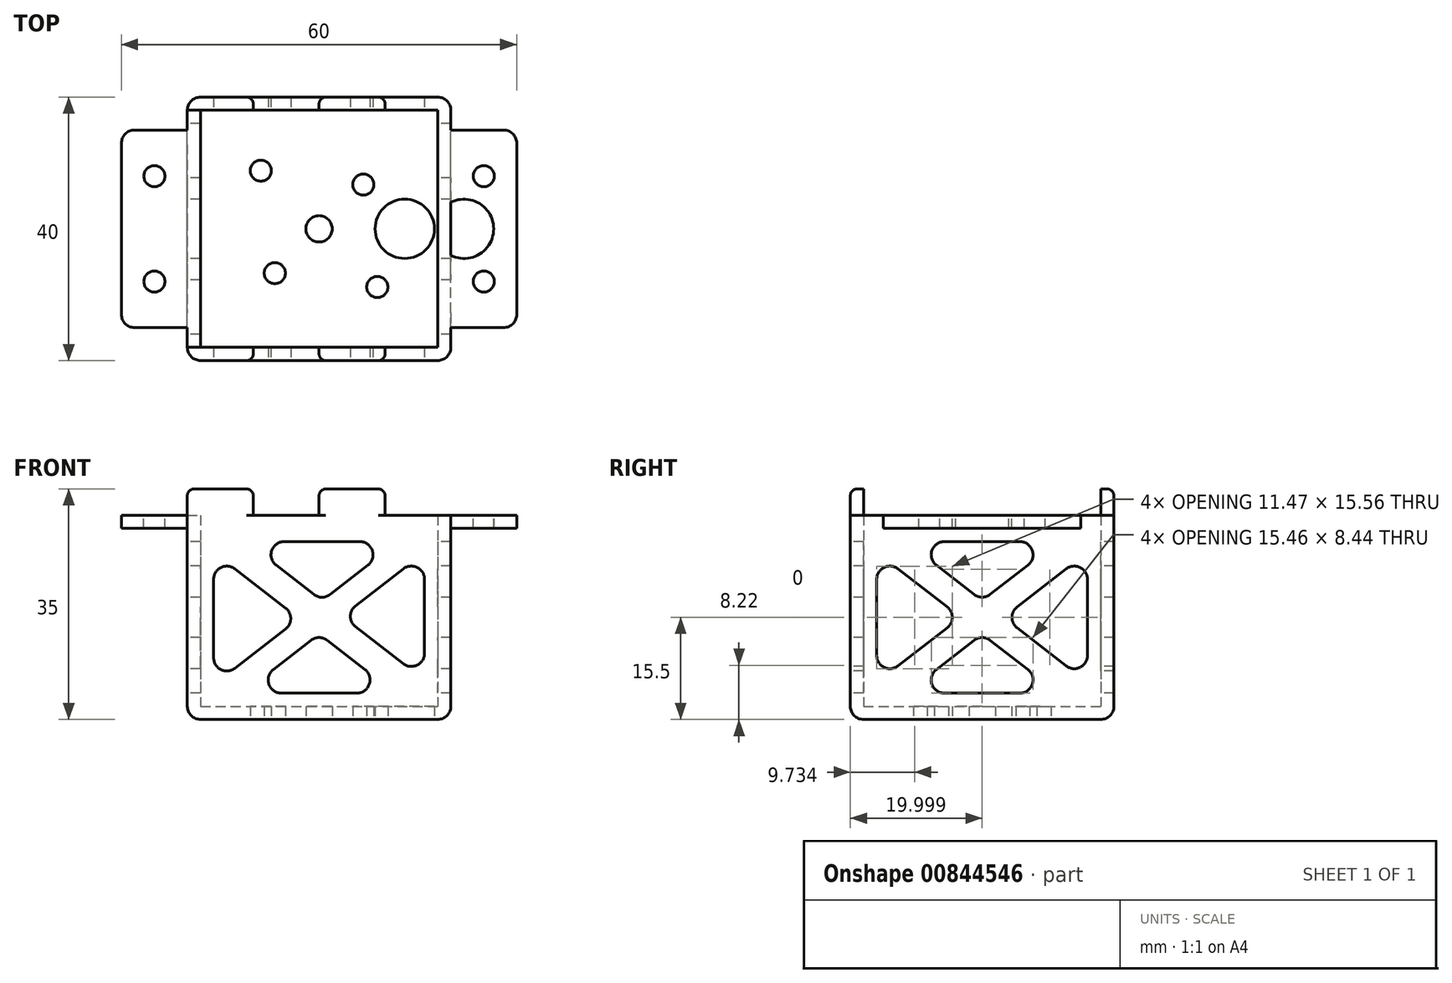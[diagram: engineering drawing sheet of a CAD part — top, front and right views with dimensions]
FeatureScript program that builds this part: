
annotation { "Feature Type Name" : "Feature", "Feature Type Description" : "" }
export const myFeature = defineFeature(function(context is Context, id is Id, definition is map)
    precondition{}
    {
        {
            var Q0;
            Q0=qCreatedBy(makeId("Top.planeOp"),FACE);
            var sketch = newSketch(context, id + "F0", { "sketchPlane" : qUnion([Q0])});
            skLineSegment(sketch, "E0.bottom", {"start": v(-66.54, 9.74) * mm, "end": v(-26.54, 9.74) * mm});
            skLineSegment(sketch, "E0.top", {"start": v(-66.54, 49.74) * mm, "end": v(-26.54, 49.74) * mm});
            skLineSegment(sketch, "E0.left", {"start": v(-66.54, 9.74) * mm, "end": v(-66.54, 49.74) * mm});
            skLineSegment(sketch, "E0.right", {"start": v(-26.54, 9.74) * mm, "end": v(-26.54, 49.74) * mm});
            skPoint(sketch, "E1", {"position": v(-46.54, 29.74) * mm});
            skPoint(sketch, "E1.positionSnap0", {"position": v(-46.54, 49.74) * mm});
            skPoint(sketch, "E1.positionSnap1", {"position": v(-26.54, 29.74) * mm});
            skPoint(sketch, "E2", {"position": v(-55.38, 38.58) * mm});
            skPoint(sketch, "E3", {"position": v(-37.7, 20.9) * mm});
            skPoint(sketch, "E4", {"position": v(-53.26, 23.02) * mm});
            skPoint(sketch, "E5", {"position": v(-39.82, 36.46) * mm});
            skPoint(sketch, "E6", {"position": v(-33.54, 29.74) * mm});
            skSolve(sketch);
        }
        {
            var Q0;
            Q0=makeQuery(id+"F0.imprint","IMPRINT",FACE,{"disambiguationData":[TD([[makeQuery(id+"F0.imprint","IMPRINT",EDGE,{"derivedFrom":sQuery(id+"F0.wireOp",EDGE,"E0.bottom")}),1.0]])]});
            extrude(context, id + "F1", {"entities" : qUnion([Q0]), "depth" : 2 * mm, "offsetDistance" : 25 * mm});
        }
        {
            var Q0;
            Q0=makeQuery(id+"F1.opExtrude","CAP_FACE",FACE,{"disambiguationData":[OSD([sQuery(id+"F0.wireOp",EDGE,"E0.bottom"),sQuery(id+"F0.wireOp",EDGE,"E0.top"),sQuery(id+"F0.wireOp",EDGE,"E0.left"),sQuery(id+"F0.wireOp",EDGE,"E0.right")])],"isStart":false});
            var sketch = newSketch(context, id + "F2", { "sketchPlane" : qUnion([Q0])});
            skLineSegment(sketch, "E7.bottom", {"start": v(-66.54, 9.74) * mm, "end": v(-26.54, 9.74) * mm});
            skLineSegment(sketch, "E7.top", {"start": v(-66.54, 49.74) * mm, "end": v(-26.54, 49.74) * mm});
            skLineSegment(sketch, "E7.left", {"start": v(-66.54, 9.74) * mm, "end": v(-66.54, 49.74) * mm});
            skLineSegment(sketch, "E7.right", {"start": v(-26.54, 9.74) * mm, "end": v(-26.54, 49.74) * mm});
            skLineSegment(sketch, "E8.0", {"start": v(-28.54, 11.74) * mm, "end": v(-28.54, 47.74) * mm});
            skLineSegment(sketch, "E8.1", {"start": v(-64.54, 11.74) * mm, "end": v(-28.54, 11.74) * mm});
            skLineSegment(sketch, "E8.2", {"start": v(-64.54, 11.74) * mm, "end": v(-64.54, 47.74) * mm});
            skLineSegment(sketch, "E8.3", {"start": v(-64.54, 47.74) * mm, "end": v(-28.54, 47.74) * mm});
            skSolve(sketch);
        }
        {
            var Q0;
            Q0=makeQuery(id+"F2.imprint","IMPRINT",FACE,{"disambiguationData":[TD([[makeQuery(id+"F2.imprint","IMPRINT",EDGE,{"derivedFrom":sQuery(id+"F2.wireOp",EDGE,"E7.bottom")}),1.0]])]});
            extrude(context, id + "F3", {"entities" : qUnion([Q0]), "operationType" : NewBodyOperationType.ADD, "depth" : 29 * mm, "offsetDistance" : 25 * mm});
        }
        {
            var Q0;
            Q0=makeQuery(id+"F3.boolean.opBoolean","MERGE",FACE,{"derivedFrom":[makeQuery(id+"F1.opExtrude","SWEPT_FACE",FACE,{"disambiguationData":[OSD([sQuery(id+"F0.wireOp",EDGE,"E0.bottom")])]}),makeQuery(id+"F3.opExtrude","SWEPT_FACE",FACE,{"disambiguationData":[OSD([sQuery(id+"F2.wireOp",EDGE,"E7.bottom")])]})]});
            var sketch = newSketch(context, id + "F4", { "sketchPlane" : qUnion([Q0])});
            skLineSegment(sketch, "E9", {"start": v(-66.54, 31) * mm, "end": v(-66.54, 35) * mm});
            skLineSegment(sketch, "E10", {"start": v(-66.54, 35) * mm, "end": v(-56.54, 35) * mm});
            skLineSegment(sketch, "E11", {"start": v(-56.54, 35) * mm, "end": v(-56.54, 31) * mm});
            skLineSegment(sketch, "E12.MirrorCS", {"start": v(-36.54, 35) * mm, "end": v(-46.54, 35) * mm});
            skLineSegment(sketch, "E13.MirrorCS", {"start": v(-46.54, 35) * mm, "end": v(-46.54, 31) * mm});
            skLineSegment(sketch, "E14.MirrorCS", {"start": v(-36.54, 31) * mm, "end": v(-36.54, 35) * mm});
            skSolve(sketch);
        }
        {
            var Q0;
            Q0=makeQuery(id+"F4.imprint","IMPRINT",FACE,{"disambiguationData":[TD([[makeQuery(id+"F4.imprint","IMPRINT",EDGE,{"derivedFrom":sQuery(id+"F4.wireOp",EDGE,"E12.MirrorCS")}),1.0]])]});
            var Q1;
            {var subQ0=sQuery(id+"F4.wireOp",EDGE,"E9");Q1=makeQuery(id+"F4.imprint","IMPRINT",FACE,{"disambiguationData":[TD([[makeQuery(id+"F4.imprint","IMPRINT",EDGE,{"derivedFrom":subQ0}),-1.0]])]});}
            var Q2;
            Q2=makeQuery(id+"F3.opExtrude","SWEPT_FACE",FACE,{"disambiguationData":[OSD([sQuery(id+"F2.wireOp",EDGE,"E8.1")])]});
            extrude(context, id + "F5", {"entities" : qUnion([Q0, Q1]), "operationType" : NewBodyOperationType.ADD, "endBound" : BoundingType.UP_TO_SURFACE, "oppositeDirection" : true, "depth" : 8.5 * mm, "endBoundEntityFace" : qUnion([Q2]), "offsetDistance" : 25 * mm});
        }
        {
            var Q0;
            Q0=makeQuery(id+"F3.boolean.opBoolean","MERGE",FACE,{"derivedFrom":[makeQuery(id+"F1.opExtrude","SWEPT_FACE",FACE,{"disambiguationData":[OSD([sQuery(id+"F0.wireOp",EDGE,"E0.top")])]}),makeQuery(id+"F3.opExtrude","SWEPT_FACE",FACE,{"disambiguationData":[OSD([sQuery(id+"F2.wireOp",EDGE,"E7.top")])]})]});
            var sketch = newSketch(context, id + "F6", { "sketchPlane" : qUnion([Q0])});
            skLineSegment(sketch, "E15", {"start": v(36.54, 31) * mm, "end": v(36.54, 35) * mm});
            skLineSegment(sketch, "E16", {"start": v(36.54, 35) * mm, "end": v(46.54, 35) * mm});
            skLineSegment(sketch, "E17", {"start": v(46.54, 35) * mm, "end": v(46.54, 31) * mm});
            skLineSegment(sketch, "E18", {"start": v(56.54, 31) * mm, "end": v(56.54, 35) * mm});
            skLineSegment(sketch, "E19", {"start": v(56.54, 35) * mm, "end": v(66.54, 35) * mm});
            skLineSegment(sketch, "E20", {"start": v(66.54, 35) * mm, "end": v(66.54, 31) * mm});
            skSolve(sketch);
        }
        {
            var Q0;
            {var subQ0=sQuery(id+"F6.wireOp",EDGE,"E15");Q0=makeQuery(id+"F6.imprint","IMPRINT",FACE,{"disambiguationData":[TD([[makeQuery(id+"F6.imprint","IMPRINT",EDGE,{"derivedFrom":subQ0}),-1.0]])]});}
            var Q1;
            {var subQ0=sQuery(id+"F6.wireOp",EDGE,"E18");Q1=makeQuery(id+"F6.imprint","IMPRINT",FACE,{"disambiguationData":[TD([[makeQuery(id+"F6.imprint","IMPRINT",EDGE,{"derivedFrom":subQ0}),-1.0]])]});}
            var Q2;
            Q2=makeQuery(id+"F3.opExtrude","SWEPT_FACE",FACE,{"disambiguationData":[OSD([sQuery(id+"F2.wireOp",EDGE,"E8.3")])]});
            extrude(context, id + "F7", {"entities" : qUnion([Q0, Q1]), "operationType" : NewBodyOperationType.ADD, "endBound" : BoundingType.UP_TO_SURFACE, "oppositeDirection" : true, "depth" : 25 * mm, "endBoundEntityFace" : qUnion([Q2]), "offsetDistance" : 25 * mm});
        }
        {
            var Q0;
            {var subQ0=sQuery(id+"F2.wireOp",EDGE,"E8.3");var subQ2=sQuery(id+"F2.wireOp",EDGE,"E8.1");var subQ5=sQuery(id+"F2.wireOp",EDGE,"E7.bottom");var subQ7=sQuery(id+"F2.wireOp",EDGE,"E8.0");var subQ9=sQuery(id+"F2.wireOp",EDGE,"E7.right");var subQ11=sQuery(id+"F2.wireOp",EDGE,"E7.top");var subQ15=makeQuery(id+"F1.opExtrude","SWEPT_FACE",FACE,{"disambiguationData":[OSD([sQuery(id+"F0.wireOp",EDGE,"E0.right")])]});var subQ17=makeQuery(id+"F1.opExtrude","SWEPT_FACE",FACE,{"disambiguationData":[OSD([sQuery(id+"F0.wireOp",EDGE,"E0.top")])]});var subQ23=sQuery(id+"F2.wireOp",EDGE,"E7.left");var subQ24=sQuery(id+"F2.wireOp",EDGE,"E8.2");Q0=makeQuery(id+"F7.boolean.opBoolean","SPLIT",FACE,{"disambiguationData":[TD([subQ15])],"derivedFrom":makeQuery(id+"F5.boolean.opBoolean","SPLIT",FACE,{"disambiguationData":[TD([subQ17])],"derivedFrom":makeQuery(id+"F3.opExtrude","CAP_FACE",FACE,{"disambiguationData":[OSD([subQ5,subQ11,subQ23,subQ9,subQ7,subQ2,subQ24,subQ0])],"isStart":false})})});}
            var sketch = newSketch(context, id + "F8", { "sketchPlane" : qUnion([Q0])});
            skLineSegment(sketch, "E21", {"start": v(-26.54, 44.74) * mm, "end": v(-16.54, 44.74) * mm});
            skLineSegment(sketch, "E22", {"start": v(-16.54, 44.74) * mm, "end": v(-16.54, 14.74) * mm});
            skLineSegment(sketch, "E23", {"start": v(-16.54, 14.74) * mm, "end": v(-26.54, 14.74) * mm});
            skPoint(sketch, "E24", {"position": v(-21.54, 21.74) * mm});
            skPoint(sketch, "E24.positionSnap0", {"position": v(-21.54, 14.74) * mm});
            skPoint(sketch, "E25", {"position": v(-21.54, 37.74) * mm});
            skPoint(sketch, "E26", {"position": v(-24.54, 29.74) * mm});
            skPoint(sketch, "E26.positionSnap0", {"position": v(-26.54, 29.74) * mm});
            skCircle(sketch, "E27", {"center": v(-24.54, 29.74) * mm, "radius": 4.5 * mm});
            skSolve(sketch);
        }
        {
            var Q0;
            {var subQ0=sQuery(id+"F8.wireOp",EDGE,"E21");Q0=makeQuery(id+"F8.imprint","IMPRINT",FACE,{"disambiguationData":[TD([[makeQuery(id+"F8.imprint","IMPRINT",EDGE,{"derivedFrom":subQ0}),-1.0]])]});}
            extrude(context, id + "F9", {"entities" : qUnion([Q0]), "operationType" : NewBodyOperationType.ADD, "oppositeDirection" : true, "depth" : 2 * mm, "offsetDistance" : 25 * mm});
        }
        {
            var Q0;
            {var subQ2=sQuery(id+"F2.wireOp",EDGE,"E8.3");var subQ4=sQuery(id+"F2.wireOp",EDGE,"E8.2");var subQ7=sQuery(id+"F2.wireOp",EDGE,"E7.top");var subQ8=sQuery(id+"F2.wireOp",EDGE,"E8.1");var subQ10=sQuery(id+"F2.wireOp",EDGE,"E7.left");var subQ13=makeQuery(id+"F1.opExtrude","SWEPT_FACE",FACE,{"disambiguationData":[OSD([sQuery(id+"F0.wireOp",EDGE,"E0.top")])]});var subQ14=sQuery(id+"F2.wireOp",EDGE,"E7.bottom");var subQ16=makeQuery(id+"F1.opExtrude","SWEPT_FACE",FACE,{"disambiguationData":[OSD([sQuery(id+"F0.wireOp",EDGE,"E0.left")])]});var subQ23=sQuery(id+"F2.wireOp",EDGE,"E8.0");var subQ24=sQuery(id+"F2.wireOp",EDGE,"E7.right");Q0=makeQuery(id+"F7.boolean.opBoolean","SPLIT",FACE,{"disambiguationData":[TD([subQ16])],"derivedFrom":makeQuery(id+"F5.boolean.opBoolean","SPLIT",FACE,{"disambiguationData":[TD([subQ13])],"derivedFrom":makeQuery(id+"F3.opExtrude","CAP_FACE",FACE,{"disambiguationData":[OSD([subQ14,subQ7,subQ10,subQ24,subQ23,subQ8,subQ4,subQ2])],"isStart":false})})});}
            var sketch = newSketch(context, id + "F10", { "sketchPlane" : qUnion([Q0])});
            skLineSegment(sketch, "E28", {"start": v(-76.54, 44.74) * mm, "end": v(-76.54, 14.74) * mm});
            skLineSegment(sketch, "E29", {"start": v(-76.54, 14.74) * mm, "end": v(-66.54, 14.74) * mm});
            skLineSegment(sketch, "E30", {"start": v(-66.54, 44.74) * mm, "end": v(-76.54, 44.74) * mm});
            skPoint(sketch, "E31", {"position": v(-71.54, 21.74) * mm});
            skPoint(sketch, "E31.positionSnap0", {"position": v(-71.54, 14.74) * mm});
            skPoint(sketch, "E32", {"position": v(-71.54, 37.74) * mm});
            skSolve(sketch);
        }
        {
            var Q0;
            Q0=makeQuery(id+"F10.imprint","IMPRINT",FACE,{"disambiguationData":[TD([[makeQuery(id+"F10.imprint","IMPRINT",EDGE,{"derivedFrom":sQuery(id+"F10.wireOp",EDGE,"E28")}),1.0]])]});
            extrude(context, id + "F11", {"entities" : qUnion([Q0]), "operationType" : NewBodyOperationType.ADD, "oppositeDirection" : true, "depth" : 2 * mm, "offsetDistance" : 25 * mm});
        }
        {
            var Q0;
            Q0=sQuery(id+"F8.wireOp",VERTEX,"E24");
            var Q1;
            Q1=sQuery(id+"F8.wireOp",VERTEX,"E25");
            var Q2;
            Q2=sQuery(id+"F10.wireOp",VERTEX,"E31");
            var Q3;
            Q3=sQuery(id+"F10.wireOp",VERTEX,"E32");
            var Q4;
            Q4=makeQuery(id+"F1.opExtrude","SWEPT_BODY",BODY,{"disambiguationData":[OSD([sQuery(id+"F0.wireOp",EDGE,"E0.bottom"),sQuery(id+"F0.wireOp",EDGE,"E0.top"),sQuery(id+"F0.wireOp",EDGE,"E0.left"),sQuery(id+"F0.wireOp",EDGE,"E0.right")])]});
            hole(context, id + "F12", {"style" : HoleStyle.SIMPLE, "endStyle" : HoleEndStyle.THROUGH, "holeDiameter" : 3.2 * mm, "majorDiameter" : 5 * mm, "isTappedThrough" : true, "tappedDepth" : 12 * mm, "tapClearance" : 3, "startFromSketch" : true, "locations" : qUnion([Q0, Q1, Q2, Q3]), "scope" : qUnion([Q4])});
        }
        {
            var Q0;
            {var subQ0=sQuery(id+"F2.wireOp",EDGE,"E7.bottom");Q0=makeQuery(id+"F5.boolean.opBoolean","MERGE",FACE,{"derivedFrom":[makeQuery(id+"F3.boolean.opBoolean","MERGE",FACE,{"derivedFrom":[makeQuery(id+"F1.opExtrude","SWEPT_FACE",FACE,{"disambiguationData":[OSD([sQuery(id+"F0.wireOp",EDGE,"E0.bottom")])]}),makeQuery(id+"F3.opExtrude","SWEPT_FACE",FACE,{"disambiguationData":[OSD([subQ0])]})]}),makeQuery(id+"F5.opExtrude","CAP_FACE",FACE,{"disambiguationData":[OSD([subQ0,sQuery(id+"F4.wireOp",EDGE,"E9"),sQuery(id+"F4.wireOp",EDGE,"E10"),sQuery(id+"F4.wireOp",EDGE,"E11")])],"isStart":true}),makeQuery(id+"F5.opExtrude","CAP_FACE",FACE,{"disambiguationData":[OSD([subQ0,sQuery(id+"F4.wireOp",EDGE,"E12.MirrorCS"),sQuery(id+"F4.wireOp",EDGE,"E13.MirrorCS"),sQuery(id+"F4.wireOp",EDGE,"E14.MirrorCS")])],"isStart":true})]});}
            var sketch = newSketch(context, id + "F13", { "sketchPlane" : qUnion([Q0])});
            skLineSegment(sketch, "E33.0", {"start": v(-59.31, 22.87) * mm, "end": v(-51.61, 16.9) * mm});
            skLineSegment(sketch, "E34.0", {"start": v(-53.06, 23.42) * mm, "end": v(-47.32, 18.97) * mm});
            skLineSegment(sketch, "E35.0", {"start": v(-59.31, 7.77) * mm, "end": v(-51.61, 13.74) * mm});
            skLineSegment(sketch, "E36.0", {"start": v(-53.5, 7.58) * mm, "end": v(-47.76, 12.02) * mm});
            skLineSegment(sketch, "E37.0", {"start": v(-51.84, 27) * mm, "end": v(-40.35, 27) * mm});
            skLineSegment(sketch, "E38.trimOffspring", {"start": v(-62.54, 21.29) * mm, "end": v(-62.54, 9.35) * mm});
            skLineSegment(sketch, "E39.trimOffspring", {"start": v(-52.27, 4) * mm, "end": v(-40.81, 4) * mm});
            skLineSegment(sketch, "E40.trimOffspring", {"start": v(-44.87, 18.97) * mm, "end": v(-39.12, 23.42) * mm});
            skLineSegment(sketch, "E41.trimOffspring", {"start": v(-45.31, 12.02) * mm, "end": v(-39.59, 7.58) * mm});
            skLineSegment(sketch, "E42.trimOffspring", {"start": v(-41.02, 17.25) * mm, "end": v(-33.76, 22.87) * mm});
            skLineSegment(sketch, "E43.trimOffspring", {"start": v(-41.02, 14.09) * mm, "end": v(-33.76, 8.46) * mm});
            skLineSegment(sketch, "E44.trimOffspring", {"start": v(-30.54, 21.29) * mm, "end": v(-30.54, 10.05) * mm});
            skPoint(sketch, "E45.visualSharp", {"position": v(-43.06, 15.67) * mm});
            skArc(sketch, "E45.filletArc", {"start": v(-41.02, 17.25) * mm, "mid": v(-41.8, 15.67) * mm, "end": v(-41.02, 14.09) * mm});
            skPoint(sketch, "E46.visualSharp", {"position": v(-46.54, 12.97) * mm});
            skArc(sketch, "E46.filletArc", {"start": v(-45.31, 12.02) * mm, "mid": v(-46.54, 12.44) * mm, "end": v(-47.76, 12.02) * mm});
            skPoint(sketch, "E47.visualSharp", {"position": v(-49.57, 15.32) * mm});
            skArc(sketch, "E47.filletArc", {"start": v(-51.61, 13.74) * mm, "mid": v(-50.84, 15.32) * mm, "end": v(-51.61, 16.9) * mm});
            skPoint(sketch, "E48.visualSharp", {"position": v(-46.1, 18.02) * mm});
            skArc(sketch, "E48.filletArc", {"start": v(-47.32, 18.97) * mm, "mid": v(-46.1, 18.55) * mm, "end": v(-44.87, 18.97) * mm});
            skPoint(sketch, "E49.visualSharp", {"position": v(-57.68, 27) * mm});
            skArc(sketch, "E49.filletArc", {"start": v(-51.84, 27) * mm, "mid": v(-53.73, 25.65) * mm, "end": v(-53.06, 23.42) * mm});
            skPoint(sketch, "E50.visualSharp", {"position": v(-34.5, 27) * mm});
            skArc(sketch, "E50.filletArc", {"start": v(-39.12, 23.42) * mm, "mid": v(-38.46, 25.65) * mm, "end": v(-40.35, 27) * mm});
            skPoint(sketch, "E51.visualSharp", {"position": v(-30.54, 25.37) * mm});
            skArc(sketch, "E51.filletArc", {"start": v(-30.54, 21.29) * mm, "mid": v(-31.66, 23.09) * mm, "end": v(-33.76, 22.87) * mm});
            skPoint(sketch, "E52.visualSharp", {"position": v(-30.54, 5.97) * mm});
            skArc(sketch, "E52.filletArc", {"start": v(-33.76, 8.46) * mm, "mid": v(-31.66, 8.25) * mm, "end": v(-30.54, 10.05) * mm});
            skPoint(sketch, "E53.visualSharp", {"position": v(-34.97, 4) * mm});
            skArc(sketch, "E53.filletArc", {"start": v(-40.81, 4) * mm, "mid": v(-38.92, 5.35) * mm, "end": v(-39.59, 7.58) * mm});
            skPoint(sketch, "E54.visualSharp", {"position": v(-58.11, 4) * mm});
            skArc(sketch, "E54.filletArc", {"start": v(-53.5, 7.58) * mm, "mid": v(-54.16, 5.35) * mm, "end": v(-52.27, 4) * mm});
            skPoint(sketch, "E55.visualSharp", {"position": v(-62.54, 5.27) * mm});
            skArc(sketch, "E55.filletArc", {"start": v(-62.54, 9.35) * mm, "mid": v(-61.42, 7.56) * mm, "end": v(-59.31, 7.77) * mm});
            skPoint(sketch, "E56.visualSharp", {"position": v(-62.54, 25.37) * mm});
            skArc(sketch, "E56.filletArc", {"start": v(-59.31, 22.87) * mm, "mid": v(-61.42, 23.09) * mm, "end": v(-62.54, 21.29) * mm});
            skSolve(sketch);
        }
        {
            var Q0;
            Q0=makeQuery(id+"F13.imprint","IMPRINT",FACE,{"disambiguationData":[TD([[makeQuery(id+"F13.imprint","IMPRINT",EDGE,{"derivedFrom":sQuery(id+"F13.wireOp",EDGE,"E36.0")}),-1.0]])]});
            var Q1;
            Q1=makeQuery(id+"F13.imprint","IMPRINT",FACE,{"disambiguationData":[TD([[makeQuery(id+"F13.imprint","IMPRINT",EDGE,{"derivedFrom":sQuery(id+"F13.wireOp",EDGE,"E33.0")}),-1.0]])]});
            var Q2;
            Q2=makeQuery(id+"F13.imprint","IMPRINT",FACE,{"disambiguationData":[TD([[makeQuery(id+"F13.imprint","IMPRINT",EDGE,{"derivedFrom":sQuery(id+"F13.wireOp",EDGE,"E34.0")}),1.0]])]});
            var Q3;
            Q3=makeQuery(id+"F13.imprint","IMPRINT",FACE,{"disambiguationData":[TD([[makeQuery(id+"F13.imprint","IMPRINT",EDGE,{"derivedFrom":sQuery(id+"F13.wireOp",EDGE,"E42.trimOffspring")}),-1.0]])]});
            var Q4;
            {var subQ0=sQuery(id+"F2.wireOp",EDGE,"E7.top");Q4=makeQuery(id+"F7.boolean.opBoolean","MERGE",FACE,{"derivedFrom":[makeQuery(id+"F3.boolean.opBoolean","MERGE",FACE,{"derivedFrom":[makeQuery(id+"F1.opExtrude","SWEPT_FACE",FACE,{"disambiguationData":[OSD([sQuery(id+"F0.wireOp",EDGE,"E0.top")])]}),makeQuery(id+"F3.opExtrude","SWEPT_FACE",FACE,{"disambiguationData":[OSD([subQ0])]})]}),makeQuery(id+"F7.opExtrude","CAP_FACE",FACE,{"disambiguationData":[OSD([subQ0,sQuery(id+"F6.wireOp",EDGE,"E15"),sQuery(id+"F6.wireOp",EDGE,"E16"),sQuery(id+"F6.wireOp",EDGE,"E17")])],"isStart":true}),makeQuery(id+"F7.opExtrude","CAP_FACE",FACE,{"disambiguationData":[OSD([subQ0,sQuery(id+"F6.wireOp",EDGE,"E18"),sQuery(id+"F6.wireOp",EDGE,"E19"),sQuery(id+"F6.wireOp",EDGE,"E20")])],"isStart":true})]});}
            extrude(context, id + "F14", {"entities" : qUnion([Q0, Q1, Q2, Q3]), "operationType" : NewBodyOperationType.REMOVE, "endBound" : BoundingType.UP_TO_SURFACE, "oppositeDirection" : true, "depth" : 25 * mm, "endBoundEntityFace" : qUnion([Q4]), "offsetDistance" : 25 * mm});
        }
        {
            var Q0;
            Q0=makeQuery(id+"F3.boolean.opBoolean","MERGE",FACE,{"derivedFrom":[makeQuery(id+"F1.opExtrude","SWEPT_FACE",FACE,{"disambiguationData":[OSD([sQuery(id+"F0.wireOp",EDGE,"E0.left")])]}),makeQuery(id+"F3.opExtrude","SWEPT_FACE",FACE,{"disambiguationData":[OSD([sQuery(id+"F2.wireOp",EDGE,"E7.left")])]})]});
            var sketch = newSketch(context, id + "F15", { "sketchPlane" : qUnion([Q0])});
            skLineSegment(sketch, "E57.0", {"start": v(-42.51, 22.87) * mm, "end": v(-35.04, 17.08) * mm});
            skLineSegment(sketch, "E58.trimOffspring", {"start": v(-28.51, 18.98) * mm, "end": v(-22.79, 23.42) * mm});
            skLineSegment(sketch, "E59.trimOffspring", {"start": v(-24.43, 17.08) * mm, "end": v(-16.96, 22.87) * mm});
            skLineSegment(sketch, "E60.trimOffspring", {"start": v(-24.43, 13.92) * mm, "end": v(-16.96, 8.13) * mm});
            skLineSegment(sketch, "E61.trimOffspring", {"start": v(-28.51, 12.02) * mm, "end": v(-22.79, 7.58) * mm});
            skLineSegment(sketch, "E62.trimOffspring", {"start": v(-36.7, 23.42) * mm, "end": v(-30.96, 18.98) * mm});
            skLineSegment(sketch, "E63.trimOffspring", {"start": v(-45.74, 21.29) * mm, "end": v(-45.74, 9.71) * mm});
            skLineSegment(sketch, "E64.trimOffspring", {"start": v(-13.74, 21.29) * mm, "end": v(-13.74, 9.71) * mm});
            skLineSegment(sketch, "E65.trimOffspring", {"start": v(-24.01, 27) * mm, "end": v(-35.47, 27) * mm});
            skLineSegment(sketch, "E66.trimOffspring", {"start": v(-36.7, 7.58) * mm, "end": v(-30.96, 12.02) * mm});
            skLineSegment(sketch, "E67.trimOffspring", {"start": v(-42.51, 8.13) * mm, "end": v(-35.04, 13.92) * mm});
            skLineSegment(sketch, "E68.trimOffspring", {"start": v(-24.01, 4) * mm, "end": v(-35.47, 4) * mm});
            skPoint(sketch, "E69.visualSharp", {"position": v(-18.17, 4) * mm});
            skArc(sketch, "E69.filletArc", {"start": v(-24.01, 4) * mm, "mid": v(-22.12, 5.35) * mm, "end": v(-22.79, 7.58) * mm});
            skPoint(sketch, "E70.visualSharp", {"position": v(-29.74, 12.97) * mm});
            skArc(sketch, "E70.filletArc", {"start": v(-28.51, 12.02) * mm, "mid": v(-29.74, 12.44) * mm, "end": v(-30.96, 12.02) * mm});
            skPoint(sketch, "E71.visualSharp", {"position": v(-41.31, 4) * mm});
            skArc(sketch, "E71.filletArc", {"start": v(-36.7, 7.58) * mm, "mid": v(-37.36, 5.35) * mm, "end": v(-35.47, 4) * mm});
            skPoint(sketch, "E72.visualSharp", {"position": v(-45.74, 25.37) * mm});
            skArc(sketch, "E72.filletArc", {"start": v(-42.51, 22.87) * mm, "mid": v(-44.62, 23.09) * mm, "end": v(-45.74, 21.29) * mm});
            skPoint(sketch, "E73.visualSharp", {"position": v(-33, 15.5) * mm});
            skArc(sketch, "E73.filletArc", {"start": v(-35.04, 13.92) * mm, "mid": v(-34.27, 15.5) * mm, "end": v(-35.04, 17.08) * mm});
            skPoint(sketch, "E74.visualSharp", {"position": v(-29.74, 18.03) * mm});
            skArc(sketch, "E74.filletArc", {"start": v(-30.96, 18.98) * mm, "mid": v(-29.74, 18.56) * mm, "end": v(-28.51, 18.98) * mm});
            skPoint(sketch, "E75.visualSharp", {"position": v(-41.31, 27) * mm});
            skArc(sketch, "E75.filletArc", {"start": v(-35.47, 27) * mm, "mid": v(-37.36, 25.65) * mm, "end": v(-36.7, 23.42) * mm});
            skPoint(sketch, "E76.visualSharp", {"position": v(-45.74, 5.63) * mm});
            skArc(sketch, "E76.filletArc", {"start": v(-45.74, 9.71) * mm, "mid": v(-44.62, 7.91) * mm, "end": v(-42.51, 8.13) * mm});
            skPoint(sketch, "E77.visualSharp", {"position": v(-18.17, 27) * mm});
            skArc(sketch, "E77.filletArc", {"start": v(-22.79, 23.42) * mm, "mid": v(-22.12, 25.65) * mm, "end": v(-24.01, 27) * mm});
            skPoint(sketch, "E78.visualSharp", {"position": v(-26.47, 15.5) * mm});
            skArc(sketch, "E78.filletArc", {"start": v(-24.43, 17.08) * mm, "mid": v(-25.2, 15.5) * mm, "end": v(-24.43, 13.92) * mm});
            skPoint(sketch, "E79.visualSharp", {"position": v(-13.74, 5.63) * mm});
            skArc(sketch, "E79.filletArc", {"start": v(-16.96, 8.13) * mm, "mid": v(-14.86, 7.91) * mm, "end": v(-13.74, 9.71) * mm});
            skPoint(sketch, "E80.visualSharp", {"position": v(-13.74, 25.37) * mm});
            skArc(sketch, "E80.filletArc", {"start": v(-13.74, 21.29) * mm, "mid": v(-14.86, 23.09) * mm, "end": v(-16.96, 22.87) * mm});
            skSolve(sketch);
        }
        {
            var Q0;
            Q0=makeQuery(id+"F15.imprint","IMPRINT",FACE,{"disambiguationData":[TD([[makeQuery(id+"F15.imprint","IMPRINT",EDGE,{"derivedFrom":sQuery(id+"F15.wireOp",EDGE,"E58.trimOffspring")}),1.0]])]});
            var Q1;
            Q1=makeQuery(id+"F15.imprint","IMPRINT",FACE,{"disambiguationData":[TD([[makeQuery(id+"F15.imprint","IMPRINT",EDGE,{"derivedFrom":sQuery(id+"F15.wireOp",EDGE,"E59.trimOffspring")}),-1.0]])]});
            var Q2;
            Q2=makeQuery(id+"F15.imprint","IMPRINT",FACE,{"disambiguationData":[TD([[makeQuery(id+"F15.imprint","IMPRINT",EDGE,{"derivedFrom":sQuery(id+"F15.wireOp",EDGE,"E61.trimOffspring")}),-1.0]])]});
            var Q3;
            Q3=makeQuery(id+"F15.imprint","IMPRINT",FACE,{"disambiguationData":[TD([[makeQuery(id+"F15.imprint","IMPRINT",EDGE,{"derivedFrom":sQuery(id+"F15.wireOp",EDGE,"E57.0")}),-1.0]])]});
            var Q4;
            Q4=makeQuery(id+"F3.boolean.opBoolean","MERGE",FACE,{"derivedFrom":[makeQuery(id+"F1.opExtrude","SWEPT_FACE",FACE,{"disambiguationData":[OSD([sQuery(id+"F0.wireOp",EDGE,"E0.right")])]}),makeQuery(id+"F3.opExtrude","SWEPT_FACE",FACE,{"disambiguationData":[OSD([sQuery(id+"F2.wireOp",EDGE,"E7.right")])]})]});
            extrude(context, id + "F16", {"entities" : qUnion([Q0, Q1, Q2, Q3]), "operationType" : NewBodyOperationType.REMOVE, "endBound" : BoundingType.UP_TO_SURFACE, "oppositeDirection" : true, "depth" : 25 * mm, "endBoundEntityFace" : qUnion([Q4]), "offsetDistance" : 25 * mm});
        }
        {
            var Q0;
            Q0=sQuery(id+"F0.wireOp",VERTEX,"E5");
            var Q1;
            Q1=sQuery(id+"F0.wireOp",VERTEX,"E2");
            var Q2;
            Q2=sQuery(id+"F0.wireOp",VERTEX,"E4");
            var Q3;
            Q3=sQuery(id+"F0.wireOp",VERTEX,"E3");
            var Q4;
            Q4=makeQuery(id+"F1.opExtrude","SWEPT_BODY",BODY,{"disambiguationData":[OSD([sQuery(id+"F0.wireOp",EDGE,"E0.bottom"),sQuery(id+"F0.wireOp",EDGE,"E0.top"),sQuery(id+"F0.wireOp",EDGE,"E0.left"),sQuery(id+"F0.wireOp",EDGE,"E0.right")])]});
            hole(context, id + "F17", {"style" : HoleStyle.SIMPLE, "endStyle" : HoleEndStyle.THROUGH, "oppositeDirection" : true, "holeDiameter" : 3.2 * mm, "majorDiameter" : 5 * mm, "isTappedThrough" : true, "tappedDepth" : 12 * mm, "tapClearance" : 3, "startFromSketch" : true, "locations" : qUnion([Q0, Q1, Q2, Q3]), "scope" : qUnion([Q4])});
        }
        {
            var Q0;
            Q0=makeQuery(id+"F1.opExtrude","CAP_EDGE",EDGE,{"disambiguationData":[OSD([sQuery(id+"F0.wireOp",EDGE,"E0.right")])],"isStart":true});
            var Q1;
            Q1=makeQuery(id+"F1.opExtrude","CAP_EDGE",EDGE,{"disambiguationData":[OSD([sQuery(id+"F0.wireOp",EDGE,"E0.top")])],"isStart":true});
            var Q2;
            Q2=makeQuery(id+"F1.opExtrude","CAP_EDGE",EDGE,{"disambiguationData":[OSD([sQuery(id+"F0.wireOp",EDGE,"E0.bottom")])],"isStart":true});
            var Q3;
            Q3=makeQuery(id+"F1.opExtrude","CAP_EDGE",EDGE,{"disambiguationData":[OSD([sQuery(id+"F0.wireOp",EDGE,"E0.left")])],"isStart":true});
            var Q4;
            Q4=makeQuery(id+"F3.boolean.opBoolean","MERGE",EDGE,{"derivedFrom":[makeQuery(id+"F1.opExtrude","SWEPT_EDGE",EDGE,{"disambiguationData":[OSD([sQuery(id+"F0.wireOp",EDGE,"E0.bottom"),sQuery(id+"F0.wireOp",EDGE,"E0.right")])]}),makeQuery(id+"F3.opExtrude","SWEPT_EDGE",EDGE,{"disambiguationData":[OSD([sQuery(id+"F2.wireOp",EDGE,"E7.bottom"),sQuery(id+"F2.wireOp",EDGE,"E7.right")])]})]});
            var Q5;
            Q5=makeQuery(id+"F3.boolean.opBoolean","MERGE",EDGE,{"derivedFrom":[makeQuery(id+"F1.opExtrude","SWEPT_EDGE",EDGE,{"disambiguationData":[OSD([sQuery(id+"F0.wireOp",EDGE,"E0.top"),sQuery(id+"F0.wireOp",EDGE,"E0.right")])]}),makeQuery(id+"F3.opExtrude","SWEPT_EDGE",EDGE,{"disambiguationData":[OSD([sQuery(id+"F2.wireOp",EDGE,"E7.top"),sQuery(id+"F2.wireOp",EDGE,"E7.right")])]})]});
            var Q6;
            Q6=makeQuery(id+"F3.boolean.opBoolean","MERGE",EDGE,{"derivedFrom":[makeQuery(id+"F1.opExtrude","SWEPT_EDGE",EDGE,{"disambiguationData":[OSD([sQuery(id+"F0.wireOp",EDGE,"E0.top"),sQuery(id+"F0.wireOp",EDGE,"E0.left")])]}),makeQuery(id+"F3.opExtrude","SWEPT_EDGE",EDGE,{"disambiguationData":[OSD([sQuery(id+"F2.wireOp",EDGE,"E7.top"),sQuery(id+"F2.wireOp",EDGE,"E7.left")])]})]});
            var Q7;
            Q7=makeQuery(id+"F11.opExtrude","SWEPT_EDGE",EDGE,{"disambiguationData":[OSD([sQuery(id+"F10.wireOp",EDGE,"E28"),sQuery(id+"F10.wireOp",EDGE,"E29")])]});
            var Q8;
            Q8=makeQuery(id+"F11.opExtrude","SWEPT_EDGE",EDGE,{"disambiguationData":[OSD([sQuery(id+"F10.wireOp",EDGE,"E28"),sQuery(id+"F10.wireOp",EDGE,"E30")])]});
            var Q9;
            Q9=makeQuery(id+"F9.opExtrude","SWEPT_EDGE",EDGE,{"disambiguationData":[OSD([sQuery(id+"F8.wireOp",EDGE,"E22"),sQuery(id+"F8.wireOp",EDGE,"E23")])]});
            var Q10;
            Q10=makeQuery(id+"F9.opExtrude","SWEPT_EDGE",EDGE,{"disambiguationData":[OSD([sQuery(id+"F8.wireOp",EDGE,"E21"),sQuery(id+"F8.wireOp",EDGE,"E22")])]});
            var Q11;
            Q11=makeQuery(id+"F5.boolean.opBoolean","MERGE",EDGE,{"derivedFrom":[makeQuery(id+"F3.boolean.opBoolean","MERGE",EDGE,{"derivedFrom":[makeQuery(id+"F1.opExtrude","SWEPT_EDGE",EDGE,{"disambiguationData":[OSD([sQuery(id+"F0.wireOp",EDGE,"E0.bottom"),sQuery(id+"F0.wireOp",EDGE,"E0.left")])]}),makeQuery(id+"F3.opExtrude","SWEPT_EDGE",EDGE,{"disambiguationData":[OSD([sQuery(id+"F2.wireOp",EDGE,"E7.bottom"),sQuery(id+"F2.wireOp",EDGE,"E7.left")])]})]}),makeQuery(id+"F5.opExtrude","CAP_EDGE",EDGE,{"disambiguationData":[OSD([sQuery(id+"F4.wireOp",EDGE,"E9")])],"isStart":true})]});
            fillet(context, id + "F18", {"entities" : qUnion([Q0, Q1, Q2, Q3, Q4, Q5, Q6, Q7, Q8, Q9, Q10, Q11]), "radius" : 2 * mm, "tangentPropagation" : true, "allowEdgeOverflow" : false});
        }
        {
            var Q0;
            Q0=makeQuery(id+"F5.opExtrude","CAP_EDGE",EDGE,{"disambiguationData":[OSD([sQuery(id+"F4.wireOp",EDGE,"E12.MirrorCS")])],"isStart":true});
            var Q1;
            Q1=makeQuery(id+"F5.opExtrude","TWEAK_EDGE",EDGE,{"derivedFrom":[makeQuery(id+"F3.opExtrude","SWEPT_FACE",FACE,{"disambiguationData":[OSD([sQuery(id+"F2.wireOp",EDGE,"E8.1")])]}),makeQuery(id+"F4.imprint","IMPRINT",EDGE,{"derivedFrom":sQuery(id+"F4.wireOp",EDGE,"E12.MirrorCS")})]});
            var Q2;
            Q2=makeQuery(id+"F5.opExtrude","CAP_EDGE",EDGE,{"disambiguationData":[OSD([sQuery(id+"F4.wireOp",EDGE,"E10")])],"isStart":true});
            var Q3;
            Q3=makeQuery(id+"F5.opExtrude","TWEAK_EDGE",EDGE,{"derivedFrom":[makeQuery(id+"F3.opExtrude","SWEPT_FACE",FACE,{"disambiguationData":[OSD([sQuery(id+"F2.wireOp",EDGE,"E8.1")])]}),makeQuery(id+"F4.imprint","IMPRINT",EDGE,{"derivedFrom":sQuery(id+"F4.wireOp",EDGE,"E10")})]});
            var Q4;
            Q4=makeQuery(id+"F7.opExtrude","TWEAK_EDGE",EDGE,{"derivedFrom":[makeQuery(id+"F3.opExtrude","SWEPT_FACE",FACE,{"disambiguationData":[OSD([sQuery(id+"F2.wireOp",EDGE,"E8.3")])]}),makeQuery(id+"F6.imprint","IMPRINT",EDGE,{"derivedFrom":sQuery(id+"F6.wireOp",EDGE,"E19")})]});
            var Q5;
            Q5=makeQuery(id+"F7.opExtrude","TWEAK_EDGE",EDGE,{"derivedFrom":[makeQuery(id+"F3.opExtrude","SWEPT_FACE",FACE,{"disambiguationData":[OSD([sQuery(id+"F2.wireOp",EDGE,"E8.3")])]}),makeQuery(id+"F6.imprint","IMPRINT",EDGE,{"derivedFrom":sQuery(id+"F6.wireOp",EDGE,"E16")})]});
            var Q6;
            Q6=makeQuery(id+"F7.opExtrude","CAP_EDGE",EDGE,{"disambiguationData":[OSD([sQuery(id+"F6.wireOp",EDGE,"E16")])],"isStart":true});
            var Q7;
            Q7=makeQuery(id+"F7.opExtrude","CAP_EDGE",EDGE,{"disambiguationData":[OSD([sQuery(id+"F6.wireOp",EDGE,"E19")])],"isStart":true});
            fillet(context, id + "F19", {"entities" : qUnion([Q0, Q1, Q2, Q3, Q4, Q5, Q6, Q7]), "radius" : 1 * mm, "tangentPropagation" : true, "allowEdgeOverflow" : false});
        }
        {
            var Q0;
            Q0=sQuery(id+"F0.wireOp",VERTEX,"E6");
            var Q1;
            Q1=makeQuery(id+"F1.opExtrude","SWEPT_BODY",BODY,{"disambiguationData":[OSD([sQuery(id+"F0.wireOp",EDGE,"E0.bottom"),sQuery(id+"F0.wireOp",EDGE,"E0.top"),sQuery(id+"F0.wireOp",EDGE,"E0.left"),sQuery(id+"F0.wireOp",EDGE,"E0.right")])]});
            hole(context, id + "F20", {"style" : HoleStyle.SIMPLE, "endStyle" : HoleEndStyle.THROUGH, "oppositeDirection" : true, "holeDiameter" : 9 * mm, "majorDiameter" : 5 * mm, "isTappedThrough" : true, "tappedDepth" : 12 * mm, "tapClearance" : 3, "startFromSketch" : true, "locations" : qUnion([Q0]), "scope" : qUnion([Q1])});
        }
        {
            var Q0;
            Q0=sQuery(id+"F0.wireOp",VERTEX,"E1");
            var Q1;
            Q1=makeQuery(id+"F1.opExtrude","SWEPT_BODY",BODY,{"disambiguationData":[OSD([sQuery(id+"F0.wireOp",EDGE,"E0.bottom"),sQuery(id+"F0.wireOp",EDGE,"E0.top"),sQuery(id+"F0.wireOp",EDGE,"E0.left"),sQuery(id+"F0.wireOp",EDGE,"E0.right")])]});
            hole(context, id + "F21", {"style" : HoleStyle.SIMPLE, "endStyle" : HoleEndStyle.THROUGH, "oppositeDirection" : true, "holeDiameter" : 4 * mm, "majorDiameter" : 5 * mm, "isTappedThrough" : true, "tappedDepth" : 12 * mm, "tapClearance" : 3, "startFromSketch" : true, "locations" : qUnion([Q0]), "scope" : qUnion([Q1])});
        }
        {
            var Q0;
            Q0=makeQuery(id+"F7.opExtrude","CAP_EDGE",EDGE,{"disambiguationData":[OSD([sQuery(id+"F6.wireOp",EDGE,"E15")])],"isStart":true});
            var Q1;
            Q1=makeQuery(id+"F7.opExtrude","TWEAK_EDGE",EDGE,{"derivedFrom":[makeQuery(id+"F3.opExtrude","SWEPT_FACE",FACE,{"disambiguationData":[OSD([sQuery(id+"F2.wireOp",EDGE,"E8.3")])]}),makeQuery(id+"F6.imprint","IMPRINT",EDGE,{"derivedFrom":sQuery(id+"F6.wireOp",EDGE,"E15")})]});
            var Q2;
            Q2=makeQuery(id+"F7.opExtrude","CAP_EDGE",EDGE,{"disambiguationData":[OSD([sQuery(id+"F6.wireOp",EDGE,"E17")])],"isStart":true});
            var Q3;
            Q3=makeQuery(id+"F7.opExtrude","TWEAK_EDGE",EDGE,{"derivedFrom":[makeQuery(id+"F3.opExtrude","SWEPT_FACE",FACE,{"disambiguationData":[OSD([sQuery(id+"F2.wireOp",EDGE,"E8.3")])]}),makeQuery(id+"F6.imprint","IMPRINT",EDGE,{"derivedFrom":sQuery(id+"F6.wireOp",EDGE,"E17")})]});
            var Q4;
            Q4=makeQuery(id+"F7.opExtrude","TWEAK_EDGE",EDGE,{"derivedFrom":[makeQuery(id+"F3.opExtrude","SWEPT_FACE",FACE,{"disambiguationData":[OSD([sQuery(id+"F2.wireOp",EDGE,"E8.3")])]}),makeQuery(id+"F6.imprint","IMPRINT",EDGE,{"derivedFrom":sQuery(id+"F6.wireOp",EDGE,"E18")})]});
            var Q5;
            Q5=makeQuery(id+"F7.opExtrude","CAP_EDGE",EDGE,{"disambiguationData":[OSD([sQuery(id+"F6.wireOp",EDGE,"E18")])],"isStart":true});
            var Q6;
            Q6=makeQuery(id+"F5.opExtrude","CAP_EDGE",EDGE,{"disambiguationData":[OSD([sQuery(id+"F4.wireOp",EDGE,"E11")])],"isStart":true});
            var Q7;
            Q7=makeQuery(id+"F5.opExtrude","CAP_EDGE",EDGE,{"disambiguationData":[OSD([sQuery(id+"F4.wireOp",EDGE,"E13.MirrorCS")])],"isStart":true});
            var Q8;
            Q8=makeQuery(id+"F5.opExtrude","CAP_EDGE",EDGE,{"disambiguationData":[OSD([sQuery(id+"F4.wireOp",EDGE,"E14.MirrorCS")])],"isStart":true});
            var Q9;
            {var subQ0=sQuery(id+"F4.wireOp",EDGE,"E14.MirrorCS");Q9=makeQuery(id+"F5.opExtrude","TWEAK_EDGE",EDGE,{"derivedFrom":[makeQuery(id+"F3.opExtrude","SWEPT_FACE",FACE,{"disambiguationData":[OSD([sQuery(id+"F2.wireOp",EDGE,"E8.1")])]}),makeQuery(id+"F4.imprint","IMPRINT",EDGE,{"disambiguationData":[TD([[makeQuery(id+"F4.imprint","INTERSECT",VERTEX,{"derivedFrom":[sQuery(id+"F4.wireOp",EDGE,"E12.MirrorCS"),subQ0]}),1.0]])],"derivedFrom":subQ0})]});}
            var Q10;
            Q10=makeQuery(id+"F5.opExtrude","TWEAK_EDGE",EDGE,{"derivedFrom":[makeQuery(id+"F3.opExtrude","SWEPT_FACE",FACE,{"disambiguationData":[OSD([sQuery(id+"F2.wireOp",EDGE,"E8.1")])]}),makeQuery(id+"F4.imprint","IMPRINT",EDGE,{"derivedFrom":sQuery(id+"F4.wireOp",EDGE,"E11")})]});
            var Q11;
            Q11=makeQuery(id+"F5.opExtrude","TWEAK_EDGE",EDGE,{"derivedFrom":[makeQuery(id+"F3.opExtrude","SWEPT_FACE",FACE,{"disambiguationData":[OSD([sQuery(id+"F2.wireOp",EDGE,"E8.1")])]}),makeQuery(id+"F4.imprint","IMPRINT",EDGE,{"derivedFrom":sQuery(id+"F4.wireOp",EDGE,"E13.MirrorCS")})]});
            fillet(context, id + "F22", {"entities" : qUnion([Q0, Q1, Q2, Q3, Q4, Q5, Q6, Q7, Q8, Q9, Q10, Q11]), "radius" : 1 * mm, "tangentPropagation" : true, "allowEdgeOverflow" : false});
        }
    });
